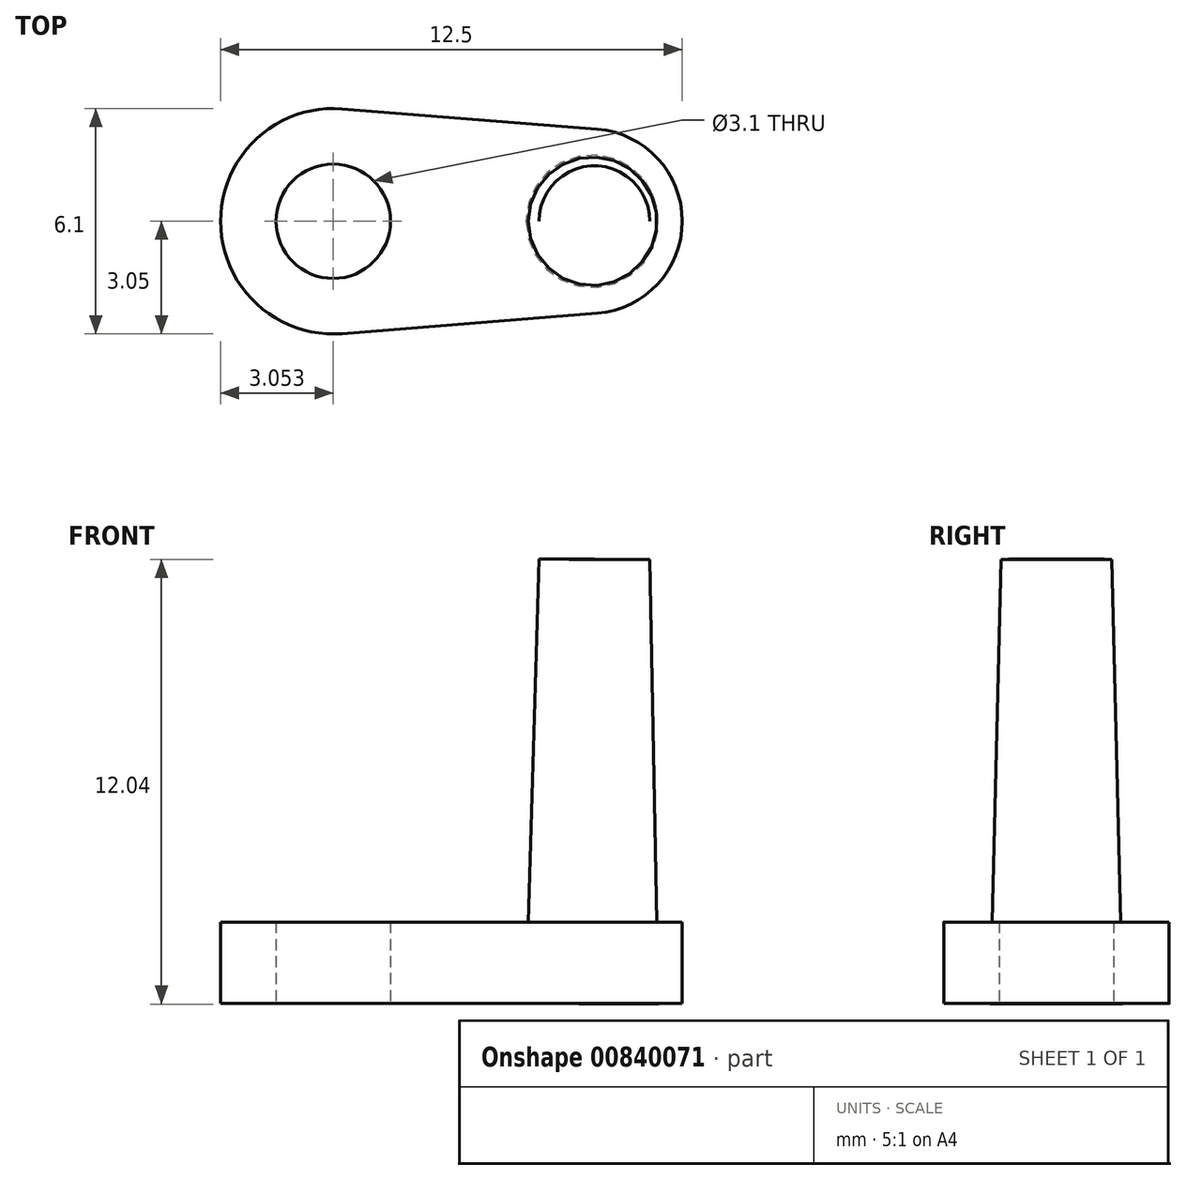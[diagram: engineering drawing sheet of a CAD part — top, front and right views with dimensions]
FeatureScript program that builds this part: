
annotation { "Feature Type Name" : "Feature", "Feature Type Description" : "" }
export const myFeature = defineFeature(function(context is Context, id is Id, definition is map)
    precondition{}
    {
        {
            var Q0;
            Q0=qCreatedBy(makeId("Top.planeOp"),FACE);
            var sketch = newSketch(context, id + "F0", { "sketchPlane" : qUnion([Q0])});
            skCircle(sketch, "E0", {"center": v(-10.04, 0) * mm, "radius": 3.05 * mm});
            skCircle(sketch, "E1", {"center": v(-3.09, 0) * mm, "radius": 2.5 * mm});
            skLineSegment(sketch, "E2", {"start": v(-9.8, 3.04) * mm, "end": v(-2.89, 2.5) * mm});
            skLineSegment(sketch, "E3", {"start": v(-2.89, -2.5) * mm, "end": v(-10.04, -3.06) * mm});
            skCircle(sketch, "E4", {"center": v(-3.09, 0) * mm, "radius": 1.55 * mm});
            skCircle(sketch, "E5", {"center": v(-10.04, 0) * mm, "radius": 1.55 * mm});
            skSolve(sketch);
        }
        {
            var Q0;
            Q0=makeQuery(id+"F0.imprint","IMPRINT",FACE,{"disambiguationData":[TD([[makeQuery(id+"F0.imprint","IMPRINT",EDGE,{"derivedFrom":sQuery(id+"F0.wireOp",EDGE,"E5")}),-1.0]])]});
            var Q1;
            Q1=makeQuery(id+"F0.imprint","IMPRINT",FACE,{"disambiguationData":[TD([[makeQuery(id+"F0.imprint","IMPRINT",EDGE,{"derivedFrom":sQuery(id+"F0.wireOp",EDGE,"E5")}),1.0]])]});
            var Q2;
            {var subQ0=sQuery(id+"F0.wireOp",EDGE,"E2");Q2=makeQuery(id+"F0.imprint","IMPRINT",FACE,{"disambiguationData":[TD([[makeQuery(id+"F0.imprint","IMPRINT",EDGE,{"derivedFrom":subQ0}),-1.0]])]});}
            var Q3;
            Q3=makeQuery(id+"F0.imprint","IMPRINT",FACE,{"disambiguationData":[TD([[makeQuery(id+"F0.imprint","IMPRINT",EDGE,{"derivedFrom":sQuery(id+"F0.wireOp",EDGE,"E4")}),-1.0]])]});
            var Q4;
            Q4=makeQuery(id+"F0.imprint","IMPRINT",FACE,{"disambiguationData":[TD([[makeQuery(id+"F0.imprint","IMPRINT",EDGE,{"derivedFrom":sQuery(id+"F0.wireOp",EDGE,"E4")}),1.0]])]});
            extrude(context, id + "F1", {"entities" : qUnion([Q0, Q1, Q2, Q3, Q4]), "depth" : 2.2 * mm, "offsetDistance" : 25 * mm});
        }
        {
            var Q0;
            Q0=makeQuery(id+"F0.imprint","IMPRINT",FACE,{"disambiguationData":[TD([[makeQuery(id+"F0.imprint","IMPRINT",EDGE,{"derivedFrom":sQuery(id+"F0.wireOp",EDGE,"E5")}),1.0]])]});
            extrude(context, id + "F2", {"entities" : qUnion([Q0]), "operationType" : NewBodyOperationType.REMOVE, "depth" : 9.2 * mm, "offsetDistance" : 25 * mm});
        }
        {
            var Q0;
            Q0=qCreatedBy(makeId("Front.planeOp"),FACE);
            var sketch = newSketch(context, id + "F3", { "sketchPlane" : qUnion([Q0])});
            skLineSegment(sketch, "E6", {"start": v(-2.96, 12.02) * mm, "end": v(-4.46, 12.02) * mm});
            skLineSegment(sketch, "E7", {"start": v(-3.02, 0) * mm, "end": v(-4.82, 0) * mm});
            skLineSegment(sketch, "E8", {"start": v(-4.82, 0) * mm, "end": v(-4.46, 12.02) * mm});
            skLineSegment(sketch, "E9", {"start": v(-2.96, 12.02) * mm, "end": v(-3.02, 0) * mm});
            skSolve(sketch);
        }
        {
            var Q0;
            Q0 = qSketchRegion(id + "F3", true);
            var Q1;
            Q1=sQuery(id+"F3.wireOp",EDGE,"E9");
            revolve(context, id + "F4", {"operationType" : NewBodyOperationType.ADD, "surfaceOperationType" : NewSurfaceOperationType.NEW, "entities" : qUnion([Q0]), "axis" : qUnion([Q1]), "revolveType" : RevolveType.FULL});
        }
    });
